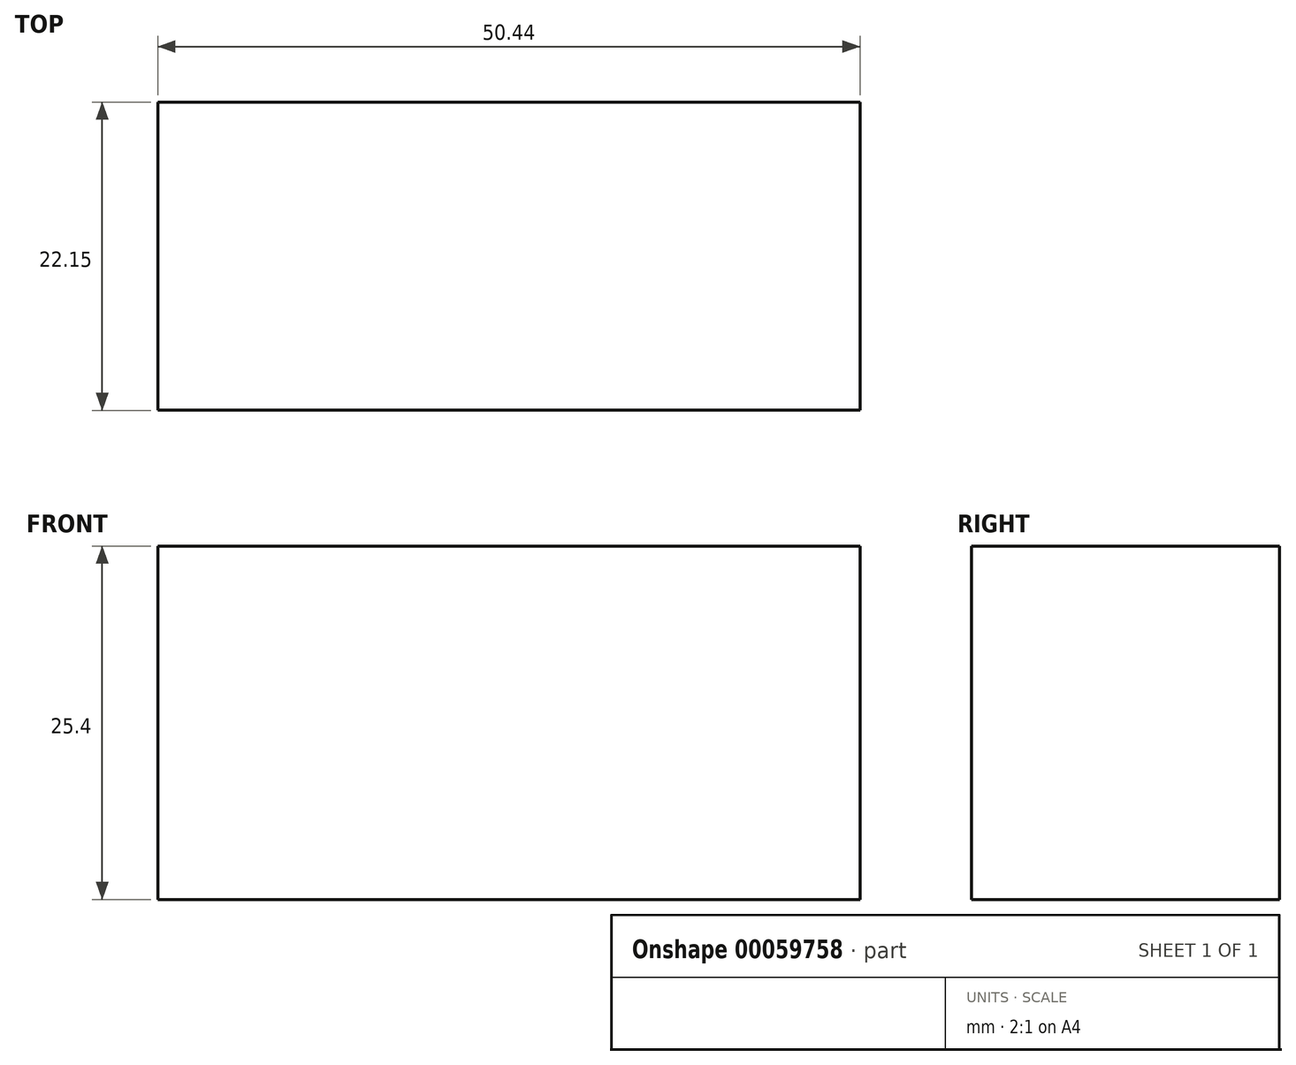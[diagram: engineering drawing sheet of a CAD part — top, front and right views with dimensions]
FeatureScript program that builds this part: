
annotation { "Feature Type Name" : "Feature", "Feature Type Description" : "" }
export const myFeature = defineFeature(function(context is Context, id is Id, definition is map)
    precondition{}
    {
        {
            var Q0;
            Q0=qCreatedBy(makeId("Top.planeOp"),FACE);
            var sketch = newSketch(context, id + "F0", { "sketchPlane" : qUnion([Q0])});
            skLineSegment(sketch, "E0.bottom", {"start": v(-56.86, -18.92) * mm, "end": v(-6.42, -18.92) * mm});
            skLineSegment(sketch, "E0.top", {"start": v(-56.86, -41.07) * mm, "end": v(-6.42, -41.07) * mm});
            skLineSegment(sketch, "E0.left", {"start": v(-56.86, -18.92) * mm, "end": v(-56.86, -41.07) * mm});
            skLineSegment(sketch, "E0.right", {"start": v(-6.42, -18.92) * mm, "end": v(-6.42, -41.07) * mm});
            skSolve(sketch);
        }
        {
            var Q0;
            Q0=makeQuery(id+"F0.imprint","IMPRINT",FACE,{"disambiguationData":[TD([[makeQuery(id+"F0.imprint","IMPRINT",EDGE,{"derivedFrom":sQuery(id+"F0.wireOp",EDGE,"E0.bottom")}),-1.0]])]});
            extrude(context, id + "F1", {"entities" : qUnion([Q0]), "oppositeDirection" : true, "depth" : 25.4 * mm});
        }
    });
